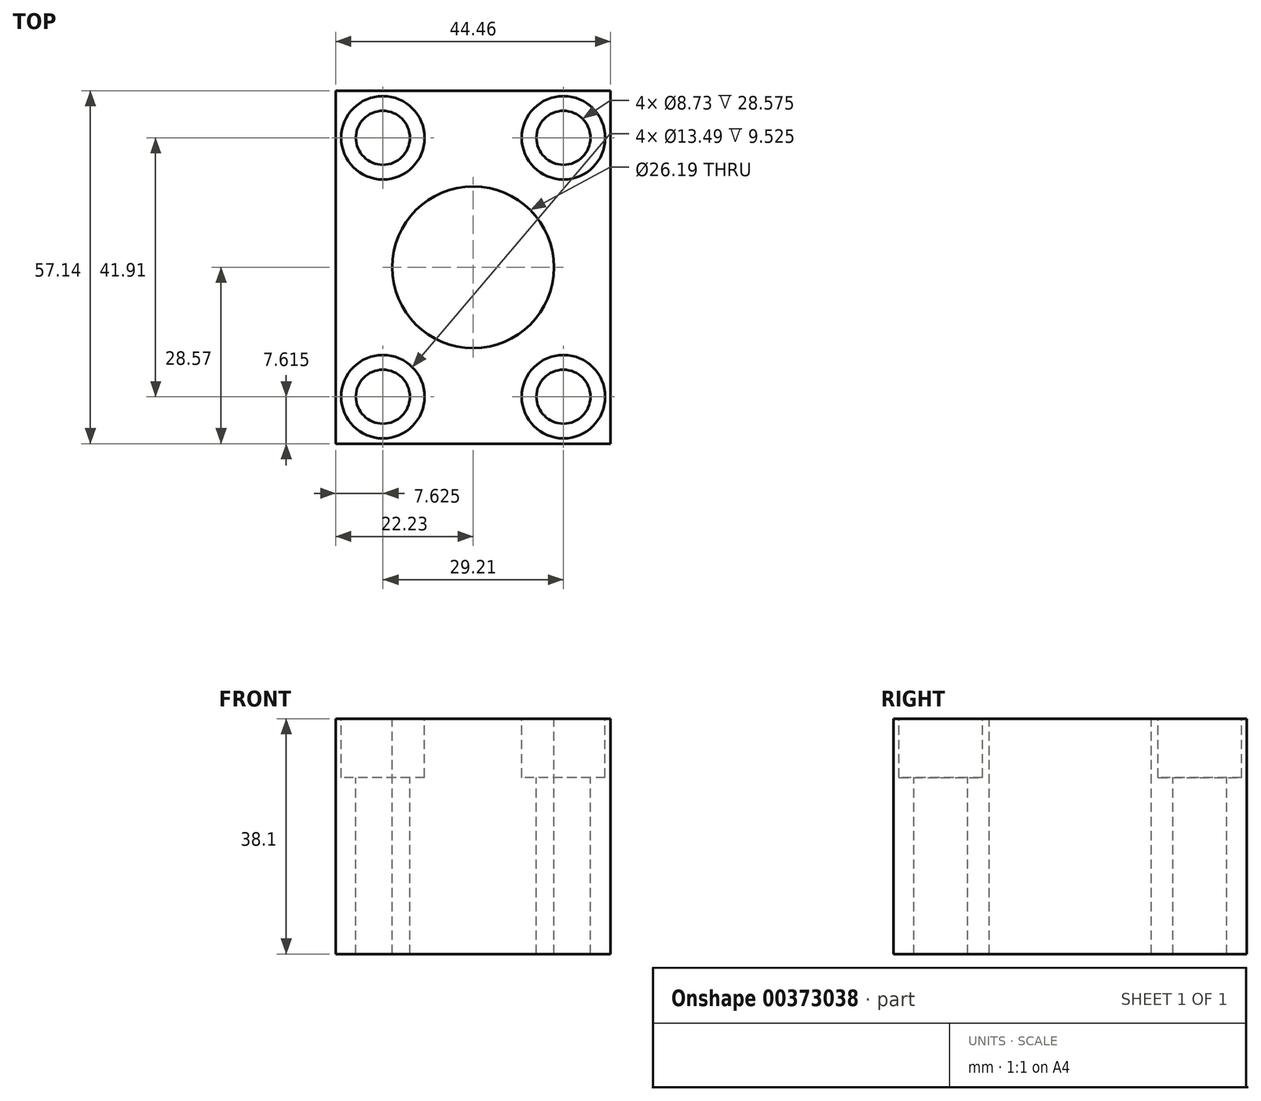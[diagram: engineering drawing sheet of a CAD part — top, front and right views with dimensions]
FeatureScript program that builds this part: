
annotation { "Feature Type Name" : "Feature", "Feature Type Description" : "" }
export const myFeature = defineFeature(function(context is Context, id is Id, definition is map)
    precondition{}
    {
        {
            var Q0;
            Q0=qCreatedBy(makeId("Top.planeOp"),FACE);
            var sketch = newSketch(context, id + "F0", { "sketchPlane" : qUnion([Q0])});
            skLineSegment(sketch, "E0.bottom", {"start": v(-22.22, 28.58) * mm, "end": v(22.23, 28.58) * mm});
            skLineSegment(sketch, "E0.top", {"start": v(-22.23, -28.58) * mm, "end": v(22.22, -28.58) * mm});
            skLineSegment(sketch, "E0.left", {"start": v(-22.22, 28.57) * mm, "end": v(-22.23, -28.58) * mm});
            skLineSegment(sketch, "E0.right", {"start": v(22.23, 28.58) * mm, "end": v(22.22, -28.58) * mm});
            skPoint(sketch, "E0.middle", {"position": v(0, 0) * mm});
            skSolve(sketch);
        }
        {
            var Q0;
            Q0 = qSketchRegion(id + "F0", true);
            extrude(context, id + "F1", {"entities" : qUnion([Q0]), "depth" : 38.1 * mm});
        }
        {
            var Q0;
            Q0=makeQuery(id+"F1.opExtrude","CAP_FACE",FACE,{"disambiguationData":[OSD([sQuery(id+"F0.wireOp",EDGE,"E0.bottom"),sQuery(id+"F0.wireOp",EDGE,"E0.top"),sQuery(id+"F0.wireOp",EDGE,"E0.left"),sQuery(id+"F0.wireOp",EDGE,"E0.right")])],"isStart":false});
            var sketch = newSketch(context, id + "F2", { "sketchPlane" : qUnion([Q0])});
            skPoint(sketch, "E1", {"position": v(0, 0) * mm});
            skSolve(sketch);
        }
        {
            var Q0;
            Q0=makeQuery(id+"F2.imprint","IMPRINT",FACE,{"disambiguationData":[TD([[makeQuery(id+"F2.imprint","IMPRINT",EDGE,{"derivedFrom":makeQuery(id+"F1.opExtrude","CAP_EDGE",EDGE,{"disambiguationData":[OSD([sQuery(id+"F0.wireOp",EDGE,"E0.bottom")])],"isStart":false})}),-1.0]])]});
            var sketch = newSketch(context, id + "F3", { "sketchPlane" : qUnion([Q0])});
            skPoint(sketch, "E2", {"position": v(0, 0) * mm});
            skSolve(sketch);
        }
        {
            var Q0;
            Q0=sQuery(id+"F2.wireOp",VERTEX,"E1");
            var Q1;
            Q1=makeQuery(id+"F1.opExtrude","SWEPT_BODY",BODY,{"disambiguationData":[OSD([sQuery(id+"F0.wireOp",EDGE,"E0.bottom"),sQuery(id+"F0.wireOp",EDGE,"E0.top"),sQuery(id+"F0.wireOp",EDGE,"E0.left"),sQuery(id+"F0.wireOp",EDGE,"E0.right")])]});
            hole(context, id + "F4", {"style" : HoleStyle.SIMPLE, "endStyle" : HoleEndStyle.THROUGH, "holeDiameter" : 26.2 * mm, "isTappedThrough" : true, "tappedDepth" : 12.7 * mm, "tapClearance" : 3, "startFromSketch" : true, "locations" : qUnion([Q0]), "scope" : qUnion([Q1])});
        }
        {
            var Q0;
            Q0=makeQuery(id+"F3.imprint","IMPRINT",FACE,{"disambiguationData":[TD([[makeQuery(id+"F3.imprint","IMPRINT",EDGE,{"derivedFrom":makeQuery(id+"F2.imprint","IMPRINT",EDGE,{"derivedFrom":makeQuery(id+"F1.opExtrude","CAP_EDGE",EDGE,{"disambiguationData":[OSD([sQuery(id+"F0.wireOp",EDGE,"E0.bottom")])],"isStart":false})})}),-1.0]])]});
            var sketch = newSketch(context, id + "F5", { "sketchPlane" : qUnion([Q0])});
            skPoint(sketch, "E3", {"position": v(-14.6, 20.96) * mm});
            skPoint(sketch, "E4.MirrorP", {"position": v(14.6, 20.96) * mm});
            skPoint(sketch, "E5.MirrorP", {"position": v(-14.6, -20.96) * mm});
            skPoint(sketch, "E6.MirrorP", {"position": v(14.6, -20.96) * mm});
            skSolve(sketch);
        }
        {
            var Q0;
            Q0=sQuery(id+"F5.wireOp",VERTEX,"E3");
            var Q1;
            Q1=sQuery(id+"F5.wireOp",VERTEX,"E4.MirrorP");
            var Q2;
            Q2=sQuery(id+"F5.wireOp",VERTEX,"E6.MirrorP");
            var Q3;
            Q3=sQuery(id+"F5.wireOp",VERTEX,"E5.MirrorP");
            var Q4;
            Q4=makeQuery(id+"F1.opExtrude","SWEPT_BODY",BODY,{"disambiguationData":[OSD([sQuery(id+"F0.wireOp",EDGE,"E0.bottom"),sQuery(id+"F0.wireOp",EDGE,"E0.top"),sQuery(id+"F0.wireOp",EDGE,"E0.left"),sQuery(id+"F0.wireOp",EDGE,"E0.right")])]});
            hole(context, id + "F6", {"style" : HoleStyle.C_BORE, "endStyle" : HoleEndStyle.THROUGH, "holeDiameter" : 8.73 * mm, "cBoreDiameter" : 13.5 * mm, "cBoreDepth" : 9.52 * mm, "isTappedThrough" : true, "tappedDepth" : 12.7 * mm, "tapClearance" : 3, "startFromSketch" : true, "locations" : qUnion([Q0, Q1, Q2, Q3]), "scope" : qUnion([Q4])});
        }
    });
